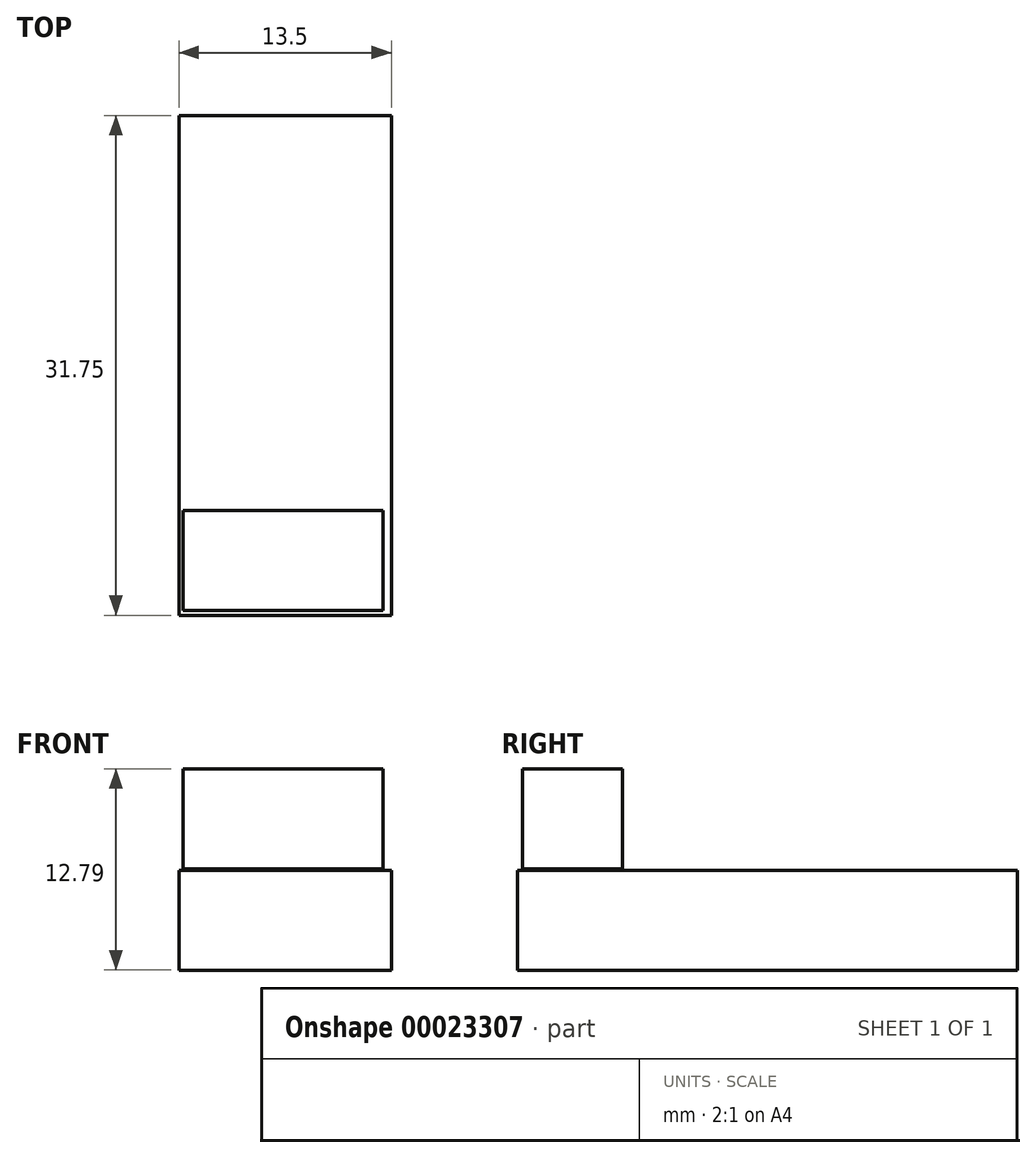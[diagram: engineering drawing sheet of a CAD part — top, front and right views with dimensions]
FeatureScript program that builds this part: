
annotation { "Feature Type Name" : "Feature", "Feature Type Description" : "" }
export const myFeature = defineFeature(function(context is Context, id is Id, definition is map)
    precondition{}
    {
        {
            var Q0;
            Q0=qCreatedBy(makeId("Front.planeOp"),FACE);
            var sketch = newSketch(context, id + "F0", { "sketchPlane" : qUnion([Q0])});
            skLineSegment(sketch, "E0.bottom", {"start": v(-10.14, 15.23) * mm, "end": v(2.56, 15.23) * mm});
            skLineSegment(sketch, "E0.top", {"start": v(-10.14, 8.88) * mm, "end": v(2.56, 8.88) * mm});
            skLineSegment(sketch, "E0.left", {"start": v(-10.14, 15.23) * mm, "end": v(-10.14, 8.88) * mm});
            skLineSegment(sketch, "E0.right", {"start": v(2.56, 15.23) * mm, "end": v(2.56, 8.88) * mm});
            skSolve(sketch);
        }
        {
            var Q0;
            Q0=makeQuery(id+"F0.imprint","IMPRINT",FACE,{"disambiguationData":[TD([[makeQuery(id+"F0.imprint","IMPRINT",EDGE,{"derivedFrom":sQuery(id+"F0.wireOp",EDGE,"E0.bottom")}),-1.0]])]});
            extrude(context, id + "F1", {"entities" : qUnion([Q0]), "depth" : 6.35 * mm});
        }
        {
            var Q0;
            Q0=qCreatedBy(makeId("Right.planeOp"),FACE);
            var sketch = newSketch(context, id + "F2", { "sketchPlane" : qUnion([Q0])});
            skLineSegment(sketch, "E1.bottom", {"start": v(-6.66, 8.79) * mm, "end": v(25.1, 8.79) * mm});
            skLineSegment(sketch, "E1.top", {"start": v(-6.66, 2.44) * mm, "end": v(25.1, 2.44) * mm});
            skLineSegment(sketch, "E1.left", {"start": v(-6.66, 8.79) * mm, "end": v(-6.66, 2.44) * mm});
            skLineSegment(sketch, "E1.right", {"start": v(25.1, 8.79) * mm, "end": v(25.1, 2.44) * mm});
            skSolve(sketch);
        }
        {
            var Q0;
            Q0=makeQuery(id+"F2.imprint","IMPRINT",FACE,{"disambiguationData":[TD([[makeQuery(id+"F2.imprint","IMPRINT",EDGE,{"derivedFrom":sQuery(id+"F2.wireOp",EDGE,"E1.bottom")}),-1.0]])]});
            extrude(context, id + "F3", {"entities" : qUnion([Q0]), "depth" : 2.77 * mm, "hasSecondDirection" : true, "secondDirectionOppositeDirection" : true, "secondDirectionDepth" : 10.42 * mm});
        }
        {
            var Q0;
            Q0=makeQuery(id+"F2.imprint","IMPRINT",FACE,{"disambiguationData":[TD([[makeQuery(id+"F2.imprint","IMPRINT",EDGE,{"derivedFrom":sQuery(id+"F2.wireOp",EDGE,"E1.bottom")}),-1.0]])]});
            extrude(context, id + "F4", {"entities" : qUnion([Q0]), "operationType" : NewBodyOperationType.ADD, "depth" : 3.08 * mm});
        }
    });
